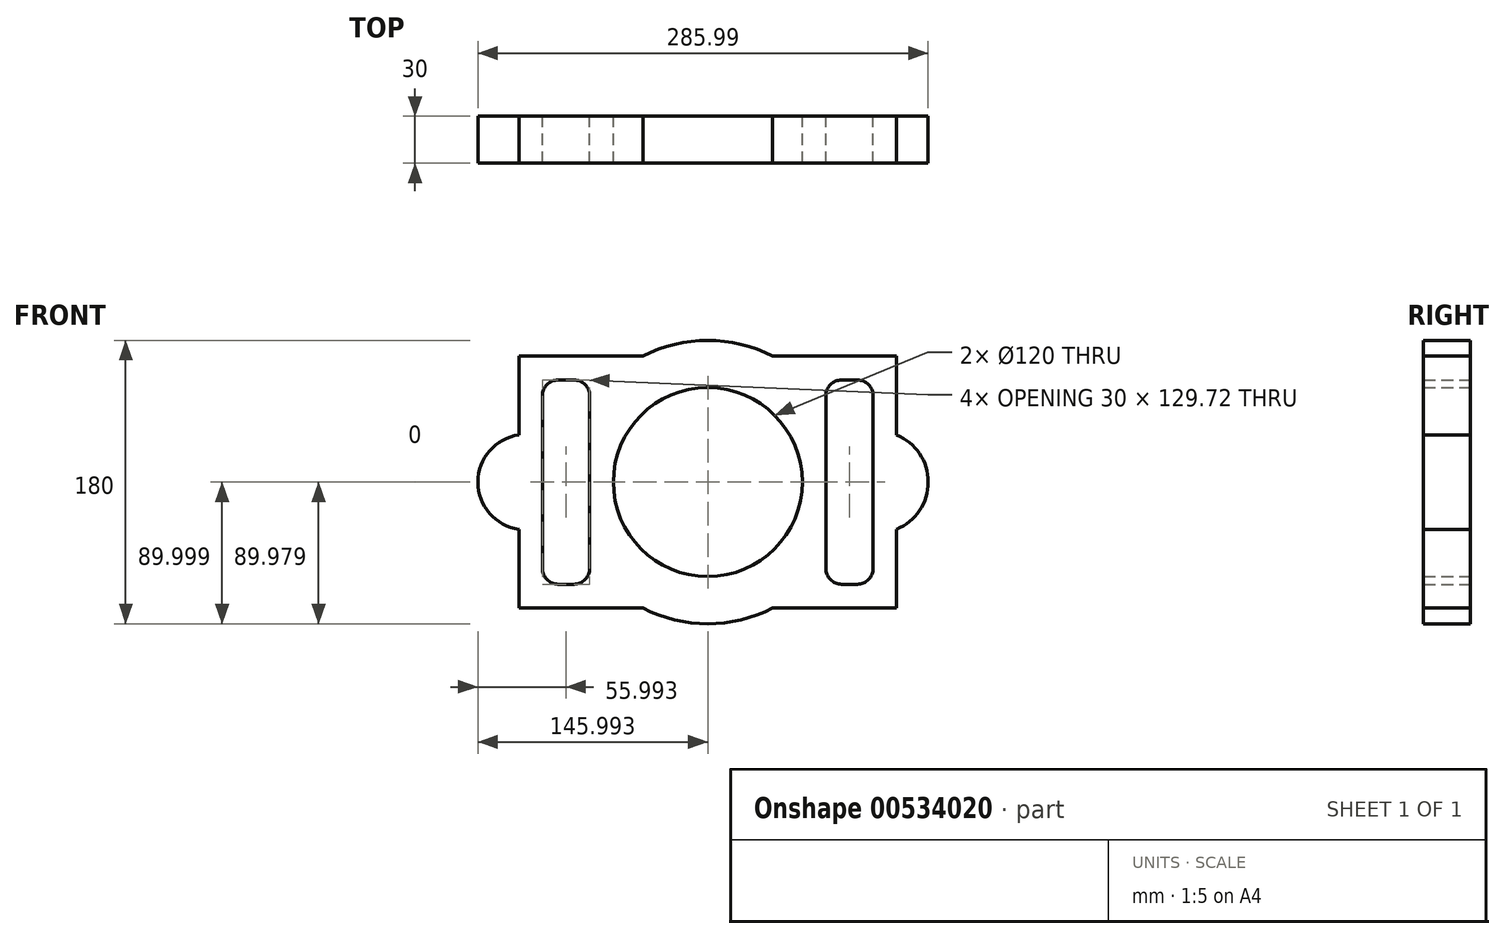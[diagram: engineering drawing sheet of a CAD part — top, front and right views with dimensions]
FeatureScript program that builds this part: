
annotation { "Feature Type Name" : "Feature", "Feature Type Description" : "" }
export const myFeature = defineFeature(function(context is Context, id is Id, definition is map)
    precondition{}
    {
        {
            var Q0;
            Q0=qCreatedBy(makeId("Front.planeOp"),FACE);
            var sketch = newSketch(context, id + "F0", { "sketchPlane" : qUnion([Q0])});
            skLineSegment(sketch, "E0", {"start": v(-93.38, 94.02) * mm, "end": v(-23.38, 94.02) * mm});
            skLineSegment(sketch, "E1", {"start": v(-23.38, 94.02) * mm, "end": v(-14.6, 94.02) * mm});
            skLineSegment(sketch, "E2", {"start": v(76.62, 94.02) * mm, "end": v(146.62, 94.02) * mm});
            skLineSegment(sketch, "E3", {"start": v(146.62, 94.02) * mm, "end": v(146.62, 44.02) * mm});
            skLineSegment(sketch, "E4", {"start": v(146.62, -15.98) * mm, "end": v(146.62, -65.98) * mm});
            skLineSegment(sketch, "E5", {"start": v(146.62, -65.98) * mm, "end": v(76.62, -65.98) * mm});
            skLineSegment(sketch, "E6", {"start": v(76.62, -65.98) * mm, "end": v(67.85, -65.98) * mm});
            skLineSegment(sketch, "E7", {"start": v(-23.38, -65.98) * mm, "end": v(-93.38, -65.98) * mm});
            skLineSegment(sketch, "E8", {"start": v(-93.38, -65.98) * mm, "end": v(-93.38, -15.98) * mm});
            skLineSegment(sketch, "E9", {"start": v(-93.38, 44.02) * mm, "end": v(-93.38, 94.02) * mm});
            skCircle(sketch, "E10", {"center": v(26.62, 14.02) * mm, "radius": 60 * mm});
            skPoint(sketch, "E11.orphan", {"position": v(-93.38, 14.02) * mm});
            skPoint(sketch, "E12.end.orphan", {"position": v(146.62, 14.02) * mm});
            skPoint(sketch, "E13.trimOffspring.end.orphan", {"position": v(26.62, -65.98) * mm});
            skPoint(sketch, "E14.start.orphan", {"position": v(26.62, 94.02) * mm});
            skArc(sketch, "E15", {"start": v(-14.6, -65.98) * mm, "mid": v(26.62, -75.98) * mm, "end": v(67.85, -65.98) * mm});
            skArc(sketch, "E16.trimOffspring", {"start": v(67.85, 94.02) * mm, "mid": v(26.62, 104.02) * mm, "end": v(-14.6, 94.02) * mm});
            skLineSegment(sketch, "E17.trimOffspring", {"start": v(67.85, 94.02) * mm, "end": v(76.62, 94.02) * mm});
            skArc(sketch, "E18", {"start": v(-93.38, 44.02) * mm, "mid": v(-119.37, 14.02) * mm, "end": v(-93.38, -15.98) * mm});
            skPoint(sketch, "E19.start.orphan", {"position": v(-119.37, 14.02) * mm});
            skArc(sketch, "E20", {"start": v(146.62, -15.98) * mm, "mid": v(166.62, 14.02) * mm, "end": v(146.62, 44.02) * mm});
            skPoint(sketch, "E21.endSnap0", {"position": v(166.62, 14.02) * mm});
            skPoint(sketch, "E21.end.orphan", {"position": v(166.62, 94.02) * mm});
            skPoint(sketch, "E21.start.orphan", {"position": v(166.62, 14.02) * mm});
            skLineSegment(sketch, "E22.trimOffspring", {"start": v(-14.6, -65.98) * mm, "end": v(-23.38, -65.98) * mm});
            skLineSegment(sketch, "E23.bottom", {"start": v(-68.38, 78.86) * mm, "end": v(-58.38, 78.86) * mm});
            skLineSegment(sketch, "E23.top", {"start": v(-68.38, -50.86) * mm, "end": v(-58.38, -50.86) * mm});
            skLineSegment(sketch, "E23.left", {"start": v(-78.38, 68.86) * mm, "end": v(-78.38, -40.86) * mm});
            skLineSegment(sketch, "E23.right", {"start": v(-48.38, 68.86) * mm, "end": v(-48.38, -40.86) * mm});
            skPoint(sketch, "E24.visualSharp", {"position": v(-78.38, 78.86) * mm});
            skArc(sketch, "E24.filletArc", {"start": v(-68.38, 78.86) * mm, "mid": v(-75.45, 75.93) * mm, "end": v(-78.38, 68.86) * mm});
            skPoint(sketch, "E25.visualSharp", {"position": v(-48.38, 78.86) * mm});
            skArc(sketch, "E25.filletArc", {"start": v(-48.38, 68.86) * mm, "mid": v(-51.3, 75.93) * mm, "end": v(-58.38, 78.86) * mm});
            skPoint(sketch, "E26.visualSharp", {"position": v(-48.38, -50.86) * mm});
            skArc(sketch, "E26.filletArc", {"start": v(-58.38, -50.86) * mm, "mid": v(-51.3, -47.93) * mm, "end": v(-48.38, -40.86) * mm});
            skPoint(sketch, "E27.visualSharp", {"position": v(-78.38, -50.86) * mm});
            skArc(sketch, "E27.filletArc", {"start": v(-78.38, -40.86) * mm, "mid": v(-75.45, -47.93) * mm, "end": v(-68.38, -50.86) * mm});
            skLineSegment(sketch, "E28.bottom", {"start": v(111.62, 78.86) * mm, "end": v(121.62, 78.86) * mm});
            skLineSegment(sketch, "E28.top", {"start": v(111.62, -50.86) * mm, "end": v(121.62, -50.86) * mm});
            skLineSegment(sketch, "E28.left", {"start": v(101.62, 68.86) * mm, "end": v(101.62, -40.86) * mm});
            skLineSegment(sketch, "E28.right", {"start": v(131.62, 68.86) * mm, "end": v(131.62, -40.86) * mm});
            skPoint(sketch, "E29.visualSharp", {"position": v(101.62, -50.86) * mm});
            skArc(sketch, "E29.filletArc", {"start": v(101.62, -40.86) * mm, "mid": v(104.55, -47.93) * mm, "end": v(111.62, -50.86) * mm});
            skPoint(sketch, "E30.visualSharp", {"position": v(131.62, -50.86) * mm});
            skArc(sketch, "E30.filletArc", {"start": v(121.62, -50.86) * mm, "mid": v(128.7, -47.93) * mm, "end": v(131.62, -40.86) * mm});
            skPoint(sketch, "E31.visualSharp", {"position": v(101.62, 78.86) * mm});
            skArc(sketch, "E31.filletArc", {"start": v(111.62, 78.86) * mm, "mid": v(104.55, 75.93) * mm, "end": v(101.62, 68.86) * mm});
            skPoint(sketch, "E32.visualSharp", {"position": v(131.62, 78.86) * mm});
            skArc(sketch, "E32.filletArc", {"start": v(131.62, 68.86) * mm, "mid": v(128.7, 75.93) * mm, "end": v(121.62, 78.86) * mm});
            skSolve(sketch);
        }
        {
            var Q0;
            Q0 = qSketchRegion(id + "F0", true);
            extrude(context, id + "F1", {"entities" : qUnion([Q0]), "depth" : 30 * mm, "offsetDistance" : 25 * mm});
        }
    });
